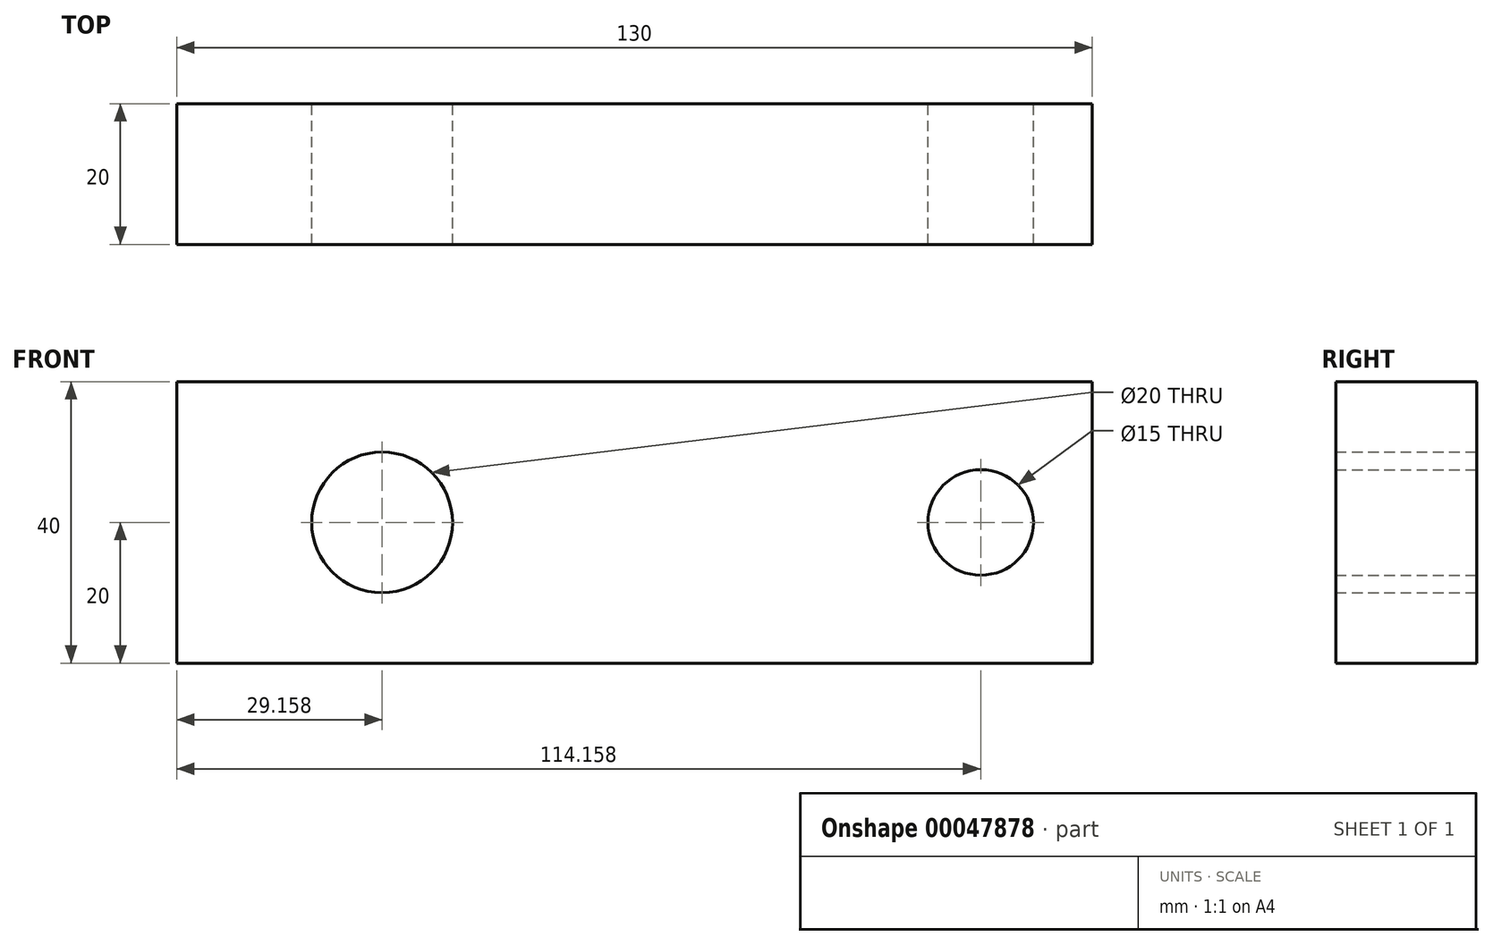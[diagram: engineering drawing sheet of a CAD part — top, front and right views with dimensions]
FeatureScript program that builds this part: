
annotation { "Feature Type Name" : "Feature", "Feature Type Description" : "" }
export const myFeature = defineFeature(function(context is Context, id is Id, definition is map)
    precondition{}
    {
        {
            var Q0;
            Q0=qCreatedBy(makeId("Front.planeOp"),FACE);
            var sketch = newSketch(context, id + "F0", { "sketchPlane" : qUnion([Q0])});
            skLineSegment(sketch, "E0.rect.bottom", {"start": v(65, 20) * mm, "end": v(-65, 20) * mm});
            skLineSegment(sketch, "E0.rect.top", {"start": v(65, -20) * mm, "end": v(-65, -20) * mm});
            skLineSegment(sketch, "E0.rect.left", {"start": v(65, 20) * mm, "end": v(65, -20) * mm});
            skLineSegment(sketch, "E0.rect.right", {"start": v(-65, 20) * mm, "end": v(-65, -20) * mm});
            skPoint(sketch, "E0.rect.middle", {"position": v(0, 0) * mm});
            skCircle(sketch, "E1", {"center": v(-35.84, 0) * mm, "radius": 10 * mm});
            skCircle(sketch, "E2", {"center": v(49.16, 0) * mm, "radius": 7.5 * mm});
            skSolve(sketch);
        }
        {
            var Q0;
            Q0=makeQuery(id+"F0.imprint","IMPRINT",FACE,{"disambiguationData":[TD([[makeQuery(id+"F0.imprint","IMPRINT",EDGE,{"derivedFrom":sQuery(id+"F0.wireOp",EDGE,"E0.rect.bottom")}),1.0]])]});
            extrude(context, id + "F1", {"entities" : qUnion([Q0]), "depth" : 20 * mm});
        }
    });
